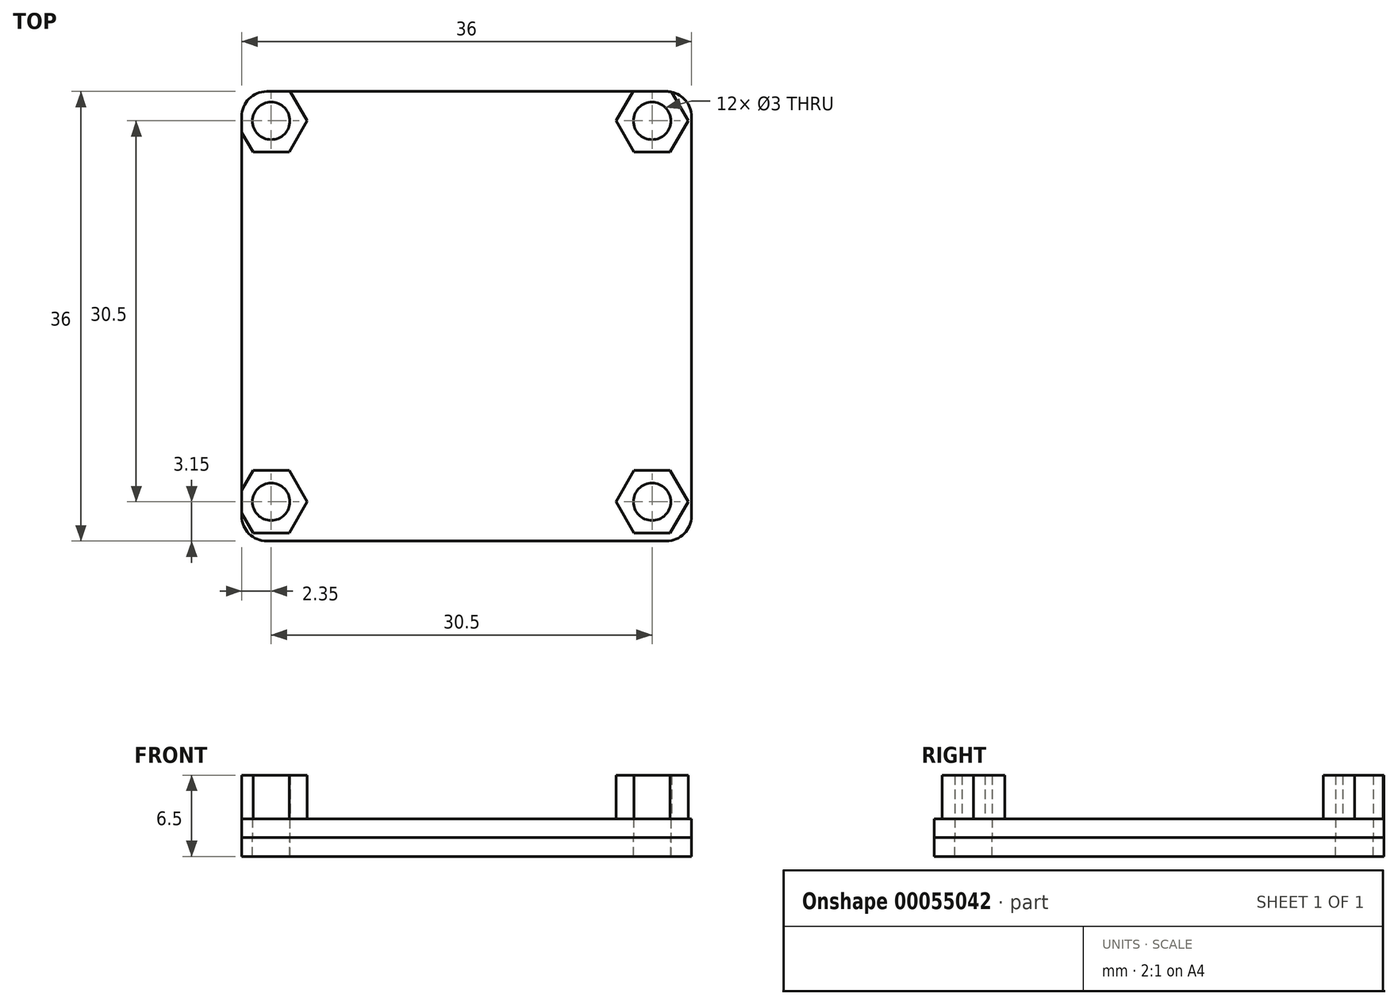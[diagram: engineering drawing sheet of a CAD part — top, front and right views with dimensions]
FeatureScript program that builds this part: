
annotation { "Feature Type Name" : "Feature", "Feature Type Description" : "" }
export const myFeature = defineFeature(function(context is Context, id is Id, definition is map)
    precondition{}
    {
        {
            var Q0;
            Q0=qCreatedBy(makeId("Top.planeOp"),FACE);
            var sketch = newSketch(context, id + "F0", { "sketchPlane" : qUnion([Q0])});
            skLineSegment(sketch, "E0.rect.bottom", {"start": v(16.4, -18.4) * mm, "end": v(-15.6, -18.4) * mm});
            skLineSegment(sketch, "E0.rect.top", {"start": v(16.4, 17.6) * mm, "end": v(-15.6, 17.6) * mm});
            skLineSegment(sketch, "E0.rect.left", {"start": v(18.4, -16.4) * mm, "end": v(18.4, 15.6) * mm});
            skLineSegment(sketch, "E0.rect.right", {"start": v(-17.6, -16.4) * mm, "end": v(-17.6, 15.6) * mm});
            skPoint(sketch, "E0.rect.middle", {"position": v(0, 0) * mm});
            skLineSegment(sketch, "E1.rect.bottom", {"start": v(15.25, -15.25) * mm, "end": v(-15.25, -15.25) * mm, "construction": true});
            skLineSegment(sketch, "E1.rect.top", {"start": v(15.25, 15.25) * mm, "end": v(-15.25, 15.25) * mm, "construction": true});
            skLineSegment(sketch, "E1.rect.left", {"start": v(15.25, -15.25) * mm, "end": v(15.25, 15.25) * mm, "construction": true});
            skLineSegment(sketch, "E1.rect.right", {"start": v(-15.25, -15.25) * mm, "end": v(-15.25, 15.25) * mm, "construction": true});
            skPoint(sketch, "E2.visualSharp", {"position": v(-17.6, 17.6) * mm});
            skArc(sketch, "E2.filletArc", {"start": v(-15.6, 17.6) * mm, "mid": v(-17.02, 17.02) * mm, "end": v(-17.6, 15.6) * mm});
            skArc(sketch, "E3.filletArc", {"start": v(18.4, 15.6) * mm, "mid": v(17.81, 17.02) * mm, "end": v(16.4, 17.6) * mm});
            skArc(sketch, "E4.filletArc", {"start": v(16.4, -18.4) * mm, "mid": v(17.81, -17.81) * mm, "end": v(18.4, -16.4) * mm});
            skArc(sketch, "E5.filletArc", {"start": v(-17.6, -16.4) * mm, "mid": v(-17.02, -17.81) * mm, "end": v(-15.6, -18.4) * mm});
            skPoint(sketch, "E6.0.midPoint", {"position": v(-15.25, 12.75) * mm});
            skPoint(sketch, "E7", {"position": v(-15.25, 15.25) * mm});
            skPoint(sketch, "E8", {"position": v(15.25, 15.25) * mm});
            skPoint(sketch, "E9", {"position": v(15.25, -15.25) * mm});
            skPoint(sketch, "E10", {"position": v(-15.25, -15.25) * mm});
            skCircle(sketch, "E11", {"center": v(-15.25, 15.25) * mm, "radius": 1.5 * mm});
            skCircle(sketch, "E12", {"center": v(15.25, 15.25) * mm, "radius": 1.5 * mm});
            skCircle(sketch, "E13", {"center": v(-15.25, -15.25) * mm, "radius": 1.5 * mm});
            skCircle(sketch, "E14", {"center": v(15.25, -15.25) * mm, "radius": 1.5 * mm});
            skSolve(sketch);
        }
        {
            var Q0;
            {var subQ0=sQuery(id+"F0.wireOp",EDGE,"067a9122-ce82-44df-8a8c-a7cc64e2cd88.5");var subQ1=sQuery(id+"F0.wireOp",EDGE,"E0.rect.left");var subQ2=makeQuery(id+"F0.imprint","INTERSECT",VERTEX,{"derivedFrom":[subQ1,subQ0]});Q0=makeQuery(id+"F0.imprint","IMPRINT",FACE,{"disambiguationData":[TD([[makeQuery(id+"F0.imprint","IMPRINT",EDGE,{"disambiguationData":[TD([[subQ2,-1.0]])],"derivedFrom":subQ1}),-1.0]])]});}
            var Q1;
            {var subQ0=sQuery(id+"F0.wireOp",EDGE,"0594f8a3-0fcc-4db6-aeb1-54b5dbc3f25d.5");var subQ1=sQuery(id+"F0.wireOp",EDGE,"E0.rect.left");var subQ2=makeQuery(id+"F0.imprint","INTERSECT",VERTEX,{"derivedFrom":[subQ1,subQ0]});Q1=makeQuery(id+"F0.imprint","IMPRINT",FACE,{"disambiguationData":[TD([[makeQuery(id+"F0.imprint","IMPRINT",EDGE,{"disambiguationData":[TD([[subQ2,-1.0]])],"derivedFrom":subQ1}),-1.0]])]});}
            var Q2;
            {var subQ0=sQuery(id+"F0.wireOp",EDGE,"93ebb783-1b2a-4d24-b839-b5876bac681c.1");var subQ1=sQuery(id+"F0.wireOp",EDGE,"E0.rect.right");var subQ2=makeQuery(id+"F0.imprint","INTERSECT",VERTEX,{"derivedFrom":[subQ1,subQ0]});Q2=makeQuery(id+"F0.imprint","IMPRINT",FACE,{"disambiguationData":[TD([[makeQuery(id+"F0.imprint","IMPRINT",EDGE,{"disambiguationData":[TD([[subQ2,-1.0]])],"derivedFrom":subQ1}),1.0]])]});}
            var Q3;
            {var subQ0=sQuery(id+"F0.wireOp",EDGE,"E6.1");var subQ1=sQuery(id+"F0.wireOp",EDGE,"E0.rect.right");var subQ2=makeQuery(id+"F0.imprint","INTERSECT",VERTEX,{"derivedFrom":[subQ1,subQ0]});Q3=makeQuery(id+"F0.imprint","IMPRINT",FACE,{"disambiguationData":[TD([[makeQuery(id+"F0.imprint","IMPRINT",EDGE,{"disambiguationData":[TD([[subQ2,-1.0]])],"derivedFrom":subQ1}),1.0]])]});}
            var Q4;
            Q4=makeQuery(id+"F0.imprint","IMPRINT",FACE,{"disambiguationData":[TD([[makeQuery(id+"F0.imprint","IMPRINT",EDGE,{"derivedFrom":sQuery(id+"F0.wireOp",EDGE,"E0.rect.bottom")}),-1.0]])]});
            extrude(context, id + "F1", {"entities" : qUnion([Q0, Q1, Q2, Q3, Q4]), "depth" : 1.5 * mm});
        }
        {
            var Q0;
            Q0=makeQuery(id+"F1.opExtrude","CAP_FACE",FACE,{"disambiguationData":[OSD([sQuery(id+"F0.wireOp",EDGE,"E0.rect.bottom"),sQuery(id+"F0.wireOp",EDGE,"E0.rect.top"),sQuery(id+"F0.wireOp",EDGE,"E0.rect.left"),sQuery(id+"F0.wireOp",EDGE,"E0.rect.right"),sQuery(id+"F0.wireOp",EDGE,"E2.filletArc"),sQuery(id+"F0.wireOp",EDGE,"E3.filletArc"),sQuery(id+"F0.wireOp",EDGE,"E4.filletArc"),sQuery(id+"F0.wireOp",EDGE,"E5.filletArc")])],"isStart":false});
            var sketch = newSketch(context, id + "F2", { "sketchPlane" : qUnion([Q0])});
            skLineSegment(sketch, "E15.rect.bottom", {"start": v(-15.25, 15.25) * mm, "end": v(15.25, 15.25) * mm});
            skLineSegment(sketch, "E15.rect.top", {"start": v(-15.25, -15.25) * mm, "end": v(15.25, -15.25) * mm});
            skLineSegment(sketch, "E15.rect.left", {"start": v(-15.25, 15.25) * mm, "end": v(-15.25, -15.25) * mm});
            skLineSegment(sketch, "E15.rect.right", {"start": v(15.25, 15.25) * mm, "end": v(15.25, -15.25) * mm});
            skPoint(sketch, "E15.rect.middle", {"position": v(0, 0) * mm});
            skCircle(sketch, "E16.cCircle", {"center": v(-15.25, 15.25) * mm, "radius": 2.5 * mm, "construction": true});
            skLineSegment(sketch, "E16.0", {"start": v(-13.8, 12.75) * mm, "end": v(-16.7, 12.75) * mm});
            skLineSegment(sketch, "E16.1", {"start": v(-16.7, 12.75) * mm, "end": v(-18.14, 15.25) * mm});
            skLineSegment(sketch, "E16.2", {"start": v(-18.14, 15.25) * mm, "end": v(-16.7, 17.75) * mm});
            skLineSegment(sketch, "E16.3", {"start": v(-16.7, 17.75) * mm, "end": v(-13.8, 17.75) * mm});
            skLineSegment(sketch, "E16.4", {"start": v(-13.8, 17.75) * mm, "end": v(-12.36, 15.25) * mm});
            skLineSegment(sketch, "E16.5", {"start": v(-12.36, 15.25) * mm, "end": v(-13.8, 12.75) * mm});
            skPoint(sketch, "E16.0.midPoint", {"position": v(-15.25, 12.75) * mm});
            skCircle(sketch, "E17.cCircle", {"center": v(15.25, 15.25) * mm, "radius": 2.5 * mm, "construction": true});
            skLineSegment(sketch, "E17.0", {"start": v(16.7, 12.75) * mm, "end": v(13.8, 12.75) * mm});
            skLineSegment(sketch, "E17.1", {"start": v(13.8, 12.75) * mm, "end": v(12.36, 15.25) * mm});
            skLineSegment(sketch, "E17.2", {"start": v(12.36, 15.25) * mm, "end": v(13.8, 17.75) * mm});
            skLineSegment(sketch, "E17.3", {"start": v(13.8, 17.75) * mm, "end": v(16.7, 17.75) * mm});
            skLineSegment(sketch, "E17.4", {"start": v(16.7, 17.75) * mm, "end": v(18.14, 15.25) * mm});
            skLineSegment(sketch, "E17.5", {"start": v(18.14, 15.25) * mm, "end": v(16.7, 12.75) * mm});
            skPoint(sketch, "E17.0.midPoint", {"position": v(15.25, 12.75) * mm});
            skCircle(sketch, "E18.cCircle", {"center": v(-15.25, -15.25) * mm, "radius": 2.5 * mm, "construction": true});
            skLineSegment(sketch, "E18.0", {"start": v(-16.7, -12.75) * mm, "end": v(-13.8, -12.75) * mm});
            skLineSegment(sketch, "E18.1", {"start": v(-13.8, -12.75) * mm, "end": v(-12.36, -15.25) * mm});
            skLineSegment(sketch, "E18.2", {"start": v(-12.36, -15.25) * mm, "end": v(-13.8, -17.75) * mm});
            skLineSegment(sketch, "E18.3", {"start": v(-13.8, -17.75) * mm, "end": v(-16.7, -17.75) * mm});
            skLineSegment(sketch, "E18.4", {"start": v(-16.7, -17.75) * mm, "end": v(-18.14, -15.25) * mm});
            skLineSegment(sketch, "E18.5", {"start": v(-18.14, -15.25) * mm, "end": v(-16.7, -12.75) * mm});
            skPoint(sketch, "E18.0.midPoint", {"position": v(-15.25, -12.75) * mm});
            skCircle(sketch, "E19.cCircle", {"center": v(15.25, -15.25) * mm, "radius": 2.5 * mm, "construction": true});
            skLineSegment(sketch, "E19.0", {"start": v(13.8, -12.75) * mm, "end": v(16.7, -12.75) * mm});
            skLineSegment(sketch, "E19.1", {"start": v(16.7, -12.75) * mm, "end": v(18.14, -15.25) * mm});
            skLineSegment(sketch, "E19.2", {"start": v(18.14, -15.25) * mm, "end": v(16.7, -17.75) * mm});
            skLineSegment(sketch, "E19.3", {"start": v(16.7, -17.75) * mm, "end": v(13.8, -17.75) * mm});
            skLineSegment(sketch, "E19.4", {"start": v(13.8, -17.75) * mm, "end": v(12.36, -15.25) * mm});
            skLineSegment(sketch, "E19.5", {"start": v(12.36, -15.25) * mm, "end": v(13.8, -12.75) * mm});
            skPoint(sketch, "E19.0.midPoint", {"position": v(15.25, -12.75) * mm});
            skSolve(sketch);
        }
        {
            var Q0;
            {var subQ0=sQuery(id+"F2.wireOp",EDGE,"E17.1");Q0=makeQuery(id+"F2.imprint","IMPRINT",FACE,{"disambiguationData":[TD([[makeQuery(id+"F2.imprint","IMPRINT",EDGE,{"derivedFrom":subQ0}),-1.0]])]});}
            var Q1;
            {var subQ0=sQuery(id+"F2.wireOp",EDGE,"E17.5");Q1=makeQuery(id+"F2.imprint","IMPRINT",FACE,{"disambiguationData":[TD([[makeQuery(id+"F2.imprint","IMPRINT",EDGE,{"derivedFrom":subQ0}),-1.0]])]});}
            var Q2;
            {var subQ0=sQuery(id+"F2.wireOp",EDGE,"E19.5");Q2=makeQuery(id+"F2.imprint","IMPRINT",FACE,{"disambiguationData":[TD([[makeQuery(id+"F2.imprint","IMPRINT",EDGE,{"derivedFrom":subQ0}),-1.0]])]});}
            var Q3;
            {var subQ0=sQuery(id+"F2.wireOp",EDGE,"E19.1");Q3=makeQuery(id+"F2.imprint","IMPRINT",FACE,{"disambiguationData":[TD([[makeQuery(id+"F2.imprint","IMPRINT",EDGE,{"derivedFrom":subQ0}),-1.0]])]});}
            var Q4;
            {var subQ0=sQuery(id+"F2.wireOp",EDGE,"E18.1");Q4=makeQuery(id+"F2.imprint","IMPRINT",FACE,{"disambiguationData":[TD([[makeQuery(id+"F2.imprint","IMPRINT",EDGE,{"derivedFrom":subQ0}),-1.0]])]});}
            var Q5;
            {var subQ0=sQuery(id+"F2.wireOp",EDGE,"E18.2");Q5=makeQuery(id+"F2.imprint","IMPRINT",FACE,{"disambiguationData":[TD([[makeQuery(id+"F2.imprint","IMPRINT",EDGE,{"derivedFrom":subQ0}),-1.0]])]});}
            var Q6;
            {var subQ0=sQuery(id+"F2.wireOp",EDGE,"E16.5");Q6=makeQuery(id+"F2.imprint","IMPRINT",FACE,{"disambiguationData":[TD([[makeQuery(id+"F2.imprint","IMPRINT",EDGE,{"derivedFrom":subQ0}),-1.0]])]});}
            var Q7;
            {var subQ7=makeQuery(id+"F1.opExtrude","CAP_EDGE",EDGE,{"disambiguationData":[OSD([sQuery(id+"F0.wireOp",EDGE,"E2.filletArc")])],"isStart":false});Q7=makeQuery(id+"F2.imprint","IMPRINT",FACE,{"disambiguationData":[TD([[makeQuery(id+"F2.imprint","IMPRINT",EDGE,{"derivedFrom":subQ7}),1.0]])]});}
            extrude(context, id + "F3", {"entities" : qUnion([Q0, Q1, Q2, Q3, Q4, Q5, Q6, Q7]), "operationType" : NewBodyOperationType.ADD, "depth" : 3.5 * mm});
        }
        {
            var Q0;
            Q0=qSketchRegion(id+"F0",true);
            var Q1;
            Q1=makeQuery(id+"F0.imprint","IMPRINT",FACE,{"disambiguationData":[TD([[makeQuery(id+"F0.imprint","IMPRINT",EDGE,{"derivedFrom":sQuery(id+"F0.wireOp",EDGE,"E0.rect.bottom")}),-1.0]])]});
            extrude(context, id + "F4", {"entities" : qUnion([Q0, Q1]), "operationType" : NewBodyOperationType.ADD, "depth" : 1.5 * mm});
        }
        {
            var Q0;
            Q0=makeQuery(id+"F0.imprint","IMPRINT",FACE,{"disambiguationData":[TD([[makeQuery(id+"F0.imprint","IMPRINT",EDGE,{"derivedFrom":sQuery(id+"F0.wireOp",EDGE,"E0.rect.bottom")}),-1.0]])]});
            extrude(context, id + "F5", {"entities" : qUnion([Q0]), "oppositeDirection" : true, "depth" : 1.5 * mm});
        }
        {
            var Q0;
            Q0=makeQuery(id+"F0.imprint","IMPRINT",FACE,{"disambiguationData":[TD([[makeQuery(id+"F0.imprint","IMPRINT",EDGE,{"derivedFrom":sQuery(id+"F0.wireOp",EDGE,"E0.rect.bottom")}),-1.0]])]});
            extrude(context, id + "F6", {"entities" : qUnion([Q0]), "depth" : 1.5 * mm, "hasSecondDirection" : true, "secondDirectionOppositeDirection" : true, "secondDirectionDepth" : 1.5 * mm});
        }
    });
